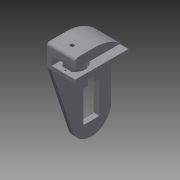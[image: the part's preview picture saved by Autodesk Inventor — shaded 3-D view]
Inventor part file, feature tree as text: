
AUTODESK INVENTOR PART (.ipt)
format: ipt  version: 2015 (Build 190159000, 159)  size: 523,776 bytes
history: native  units: mm
features: sketch x36, extrude x32, fillet x4
ambient origin geometry x8: Origin, YZ Plane, XZ Plane, XY Plane, X Axis, Y Axis, Z Axis, Center Point
bodies: Solid1 (feature_tree)
feature tree (72):
  extrude  "Extrusion1"  Depth=66.3mm
  extrude  "Extrusion2"  Depth=55.0mm
  extrude  "Extrusion3"  Depth=55.0mm
  extrude  "Extrusion4"  Depth=9.9mm
  extrude  "Extrusion5"  Depth=9.9mm
  extrude  "Extrusion6"  Depth=3.0mm
  extrude  "Extrusion7"  Depth=3.0mm
  extrude  "Extrusion8"  Depth=13.6mm
  extrude  "Extrusion9"  Depth=45.0mm
  sketch  "Sketch10"  dims[d22=15.0mm d23=5.0mm d24=0.0mm]
  extrude  "Extrusion10"  Depth=5.0mm TaperAngle=0.0deg
  extrude  "Extrusion11"  Depth=55.0mm
  extrude  "Extrusion12"  Depth=20.0mm
  sketch  "Sketch14"  dims[d33=10.0mm d34=32.9mm d35=0.0mm]
  extrude  "Extrusion13"  Depth=5.0mm TaperAngle=0.0deg
  extrude  "Extrusion14"  Depth=10.0mm TaperAngle=0.0deg
  extrude  "Extrusion15"  Depth=25.0mm
  extrude  "Extrusion16"  Depth=10.0mm TaperAngle=0.0deg
  extrude  "Extrusion17"  Depth=15.0mm
  sketch  "Sketch20"  dims[d50=28.0mm d51=5.0mm d52=0.0mm]
  extrude  "Extrusion18"  Depth=10.0mm
  extrude  "Extrusion19"  Depth=32.9mm TaperAngle=0.0deg
  extrude  "Extrusion20"  Depth=5.0mm TaperAngle=0.0deg
  extrude  "Extrusion21"  Depth=10.0mm
  extrude  "Extrusion22"  Depth=13.6mm
  extrude  "Extrusion23"  Depth=10.0mm
  sketch  "Sketch27"  dims[d68=21.4mm d69=2.0mm]
  extrude  "Extrusion24"  Depth=12.2mm
  extrude  "Extrusion25"  Depth=5.0mm TaperAngle=0.0deg
  extrude  "Extrusion26"  Depth=2.0mm
  extrude  "Extrusion27"  Depth=2.0mm
  sketch  "Sketch32"  dims[d86=5.0mm d87=5.0mm]
  sketch  "Sketch33"  dims[d88=39.0mm d89=0.0mm]
  extrude  "Extrusion28"  Depth=2.05mm
  extrude  "Extrusion29"  Depth=5.0mm TaperAngle=0.0deg
  extrude  "Extrusion30"  Depth=2.05mm
  extrude  "Extrusion31"  Depth=2.0mm
  fillet  "Fillet1"  Radius=2.05mm
  fillet  "Fillet2"  Radius=2.0mm
  fillet  "Fillet3"  Radius=5.0mm
  fillet  "Fillet4"  Radius=45.0mm
  extrude  "Extrusion34"  Depth=5.0mm
  sketch  "Sketch1"  dims[d0=33.15mm d2=66.3mm]
  sketch  "Sketch2"  dims[d4=18.1mm d5=55.0mm]
  sketch  "Sketch3"  dims[d6=20.0mm d7=55.0mm]
  sketch  "Sketch4"  dims[d8=40.2mm d9=9.9mm]
  sketch  "Sketch5"  dims[d10=9.5mm d11=9.9mm]
  sketch  "Sketch6"  dims[d12=9.5mm d13=3.0mm]
  sketch  "Sketch7"  dims[d14=3.0mm d15=3.0mm]
  sketch  "Sketch8"  dims[d16=3.0mm d17=13.6mm]
  sketch  "Sketch9"  dims[d20=25.0mm d21=45.0mm]
  sketch  "Sketch11"  dims[d25=18.1mm d26=55.0mm]
  sketch  "Sketch12"  dims[d27=40.2mm d28=20.0mm]
  sketch  "Sketch13"  dims[d29=5.0mm d30=0.0mm d31=5.0mm d32=0.0mm]
  sketch  "Sketch15"  dims[d36=25.0mm d37=0.0mm d38=25.0mm]
  sketch  "Sketch16"  dims[d39=10.0mm d40=5.0mm d41=0.0mm]
  sketch  "Sketch17"  dims[d42=12.5mm d43=15.0mm]
  sketch  "Sketch18"  dims[d44=10.0mm d45=0.0mm d46=18.0mm]
  sketch  "Sketch19"  dims[d47=5.0mm d48=32.9mm d49=0.0mm]
  sketch  "Sketch21"  dims[d53=10.0mm d54=0.0mm d55=5.0mm]
  sketch  "Sketch22"  dims[d56=12.5mm d57=13.6mm]
  sketch  "Sketch23"  dims[d58=10.0mm d59=0.0mm d60=12.5mm]
  sketch  "Sketch24"  dims[d61=12.4mm d62=12.2mm]
  sketch  "Sketch25"  dims[d63=6.2mm d64=5.0mm d65=0.0mm]
  sketch  "Sketch26"  dims[d66=10.6mm d67=2.0mm]
  sketch  "Sketch28"  dims[d70=5.0mm d71=0.0mm d72=2.05mm]
  sketch  "Sketch29"  dims[d73=2.05mm d74=5.0mm d75=0.0mm]
  sketch  "Sketch30"  dims[d76=21.4mm d77=2.05mm]
  sketch  "Sketch31"  dims[d78=2.0mm d79=10.6mm d80=2.05mm d81=2.0mm d82=5.0mm d83=0.0mm d84=45.0mm]
  sketch  "Sketch34"  dims[d90=22.0mm]
  sketch  "Sketch35"  dims[d91=5.0mm d92=0.0mm]
  sketch  "Sketch38"  dims[d93=3.0mm d94=0.0mm d95=10.0mm d96=2.0mm d97=0.0mm d98=2.0mm d99=0.0mm d100=10.25mm d101=7.25mm d102=22.0mm d103=0.0mm d104=10.0mm d105=2.0mm d106=0.0mm d107=10.0mm d108=3.0mm d109=0.0mm d111=14.0mm d112=14.0mm d113=5.0mm d114=0.0mm d115=29.9mm d116=0.0mm d117=70.0mm d118=0.0mm d119=68.0mm d120=2.0mm d121=5.0mm d122=37.9mm d123=0.0mm d124=28.0mm d125=70.0mm d126=25.0mm d127=25.0mm d128=50.0mm d129=37.9mm d130=0.0mm d131=8.0mm d132=0.0mm d133=12.0mm d134=90.0deg d135=29.9mm d136=0.0mm d137=47.0mm d138=8.0mm d139=8.0mm d140=0.0mm d141=1.0mm d149=4.0mm d150=2.0mm d151=2.0mm d153=6.2mm d154=5.0mm d155=12.0mm d156=0.0mm]
